# Revit family: Shower-GROHE-Metal_Hose-28025_Series
name_source: partatom
category: Pipe Accessories
revit_build: Autodesk Revit 2014 (Build: 20130308_1515(x64)
units: mm (PartAtom-declared; Revit-internal decimal feet)

## types (3) — shared parameters
Assembly Code = D2090800
Connection Diameter = 1/2"
Default Elevation = 0"
Description = Metal Hose 1750mm
Height = 68 29/32"
Installation Type = Surface Mounted
Manufacturer = GROHE
Price = Prices may vary. Please consult Manufacturer Representative for most up-to-date price list.
Product Page URL = http://www.grohe.com
URL = http://www.grohe.com
Warranty Information = Limited Lifetime Warranty
Width = 1/2"

## per-type parameters (varying)
| type | Finish | Material |
| 28025DA0 | Brass-Grohe-DA0-Warm Sunset | Brass-Grohe-DA0-Warm Sunset |
| 28025000 | Brass-Grohe-000-Starlight Chrome | Brass-Grohe-000-Starlight Chrome |
| 28025ZB0 | Brass-Grohe-ZB0-Oil Rubbed Bronze | Brass-Grohe-ZB0-Oil Rubbed Bronze |

note: column(s) folded — value = type name in every type: Model

## geometry (parser evidence)
native form markers: Sweep x1
no freeform markers — native parametric forms only
